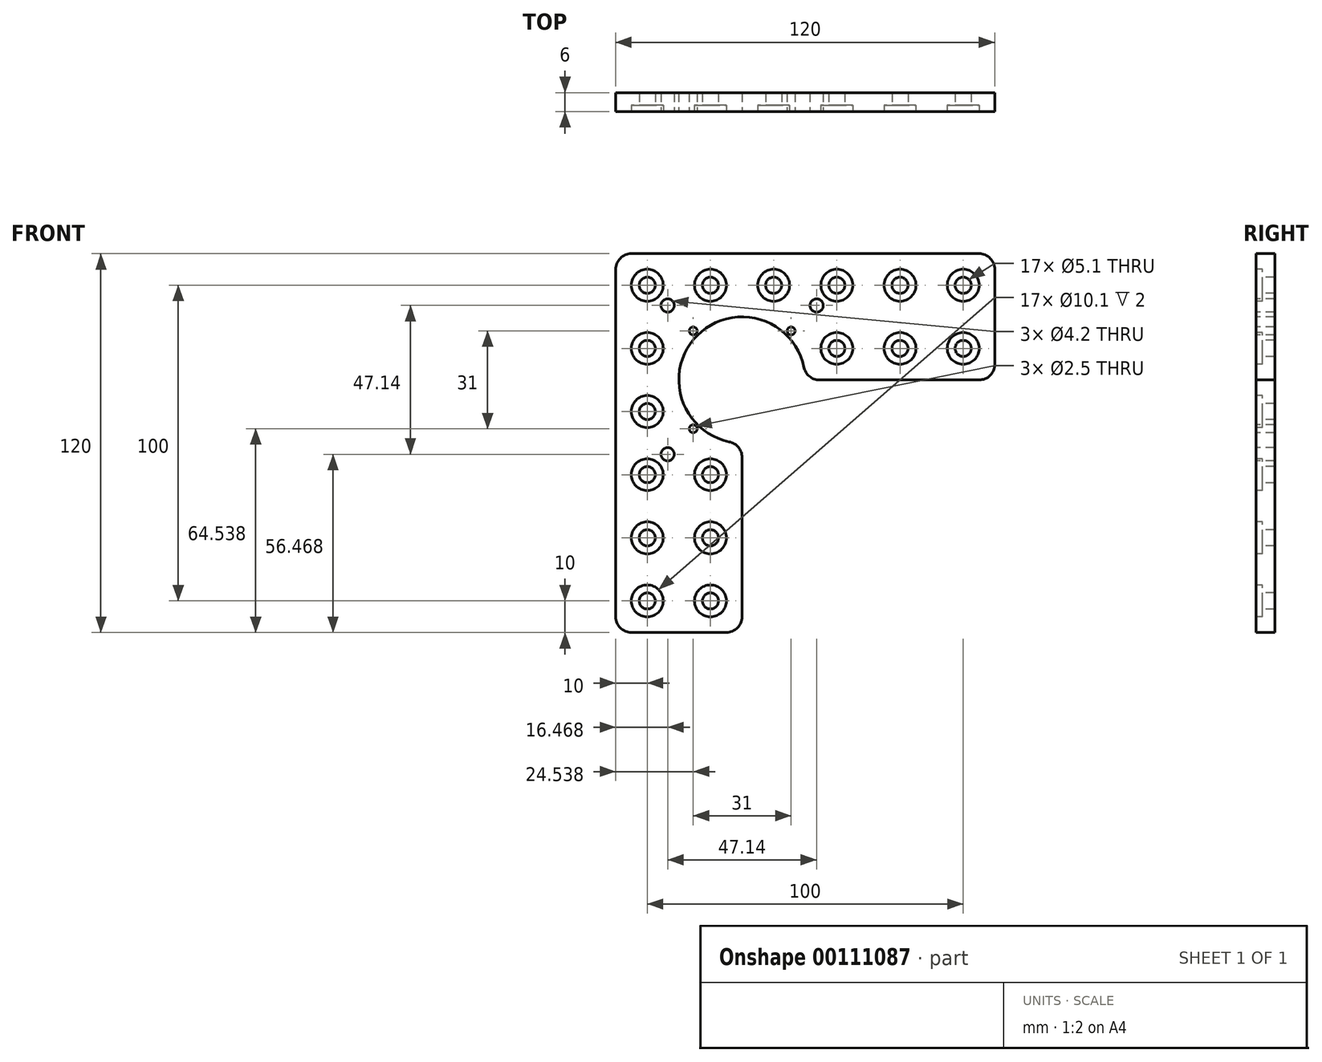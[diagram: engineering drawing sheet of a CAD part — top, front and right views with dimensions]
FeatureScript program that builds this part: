
annotation { "Feature Type Name" : "Feature", "Feature Type Description" : "" }
export const myFeature = defineFeature(function(context is Context, id is Id, definition is map)
    precondition{}
    {
        {
            var Q0;
            Q0=qCreatedBy(makeId("Front.planeOp"),FACE);
            var sketch = newSketch(context, id + "F0", { "sketchPlane" : qUnion([Q0])});
            skLineSegment(sketch, "E0.bottom", {"start": v(5, 0) * mm, "end": v(115, 0) * mm});
            skLineSegment(sketch, "E0.top", {"start": v(5, -120) * mm, "end": v(35, -120) * mm});
            skLineSegment(sketch, "E0.left", {"start": v(0, -5) * mm, "end": v(0, -115) * mm});
            skLineSegment(sketch, "E0.right", {"start": v(120, -5) * mm, "end": v(120, -35) * mm});
            skPoint(sketch, "E1", {"position": v(10, -10) * mm});
            skPoint(sketch, "E2", {"position": v(16.47, -16.4) * mm});
            skPoint(sketch, "E3", {"position": v(24.54, -24.46) * mm});
            skPoint(sketch, "E4.0.1.0", {"position": v(24.54, -55.46) * mm});
            skPoint(sketch, "E4.1.0.0", {"position": v(55.54, -24.46) * mm});
            skLineSegment(sketch, "E4.direction1", {"start": v(24.54, -24.46) * mm, "end": v(55.54, -24.46) * mm, "construction": true});
            skLineSegment(sketch, "E4.direction2", {"start": v(24.54, -24.46) * mm, "end": v(24.54, -55.46) * mm, "construction": true});
            skPoint(sketch, "E5.0.1.0", {"position": v(16.47, -63.53) * mm});
            skPoint(sketch, "E5.1.0.0", {"position": v(63.6, -16.4) * mm});
            skLineSegment(sketch, "E5.direction1", {"start": v(16.47, -16.4) * mm, "end": v(63.6, -16.4) * mm, "construction": true});
            skLineSegment(sketch, "E5.direction2", {"start": v(16.47, -16.4) * mm, "end": v(16.47, -63.53) * mm, "construction": true});
            skArc(sketch, "E6", {"start": v(59.6, -36) * mm, "mid": v(25.86, -25.86) * mm, "end": v(36, -59.6) * mm});
            skPoint(sketch, "E7.0.1.0", {"position": v(10, -30) * mm});
            skPoint(sketch, "E7.0.2.0", {"position": v(10, -50) * mm});
            skPoint(sketch, "E7.0.3.0", {"position": v(10, -70) * mm});
            skPoint(sketch, "E7.0.4.0", {"position": v(10, -90) * mm});
            skPoint(sketch, "E7.0.5.0", {"position": v(10, -110) * mm});
            skPoint(sketch, "E7.1.0.0", {"position": v(30, -10) * mm});
            skPoint(sketch, "E7.1.3.0", {"position": v(30, -70) * mm});
            skPoint(sketch, "E7.1.4.0", {"position": v(30, -90) * mm});
            skPoint(sketch, "E7.1.5.0", {"position": v(30, -110) * mm});
            skPoint(sketch, "E7.2.0.0", {"position": v(50, -10) * mm});
            skPoint(sketch, "E7.3.0.0", {"position": v(70, -10) * mm});
            skPoint(sketch, "E7.3.1.0", {"position": v(70, -30) * mm});
            skPoint(sketch, "E7.4.0.0", {"position": v(90, -10) * mm});
            skPoint(sketch, "E7.4.1.0", {"position": v(90, -30) * mm});
            skPoint(sketch, "E7.5.0.0", {"position": v(110, -10) * mm});
            skPoint(sketch, "E7.5.1.0", {"position": v(110, -30) * mm});
            skLineSegment(sketch, "E7.direction1", {"start": v(10, -10) * mm, "end": v(30, -10) * mm, "construction": true});
            skLineSegment(sketch, "E7.direction2", {"start": v(10, -10) * mm, "end": v(10, -30) * mm, "construction": true});
            skLineSegment(sketch, "E8.top", {"start": v(115, -40) * mm, "end": v(64.5, -40) * mm});
            skLineSegment(sketch, "E8.right", {"start": v(40, -115) * mm, "end": v(40, -64.5) * mm});
            skPoint(sketch, "E9.visualSharp", {"position": v(40, -120) * mm});
            skArc(sketch, "E9.filletArc", {"start": v(35, -120) * mm, "mid": v(38.54, -118.54) * mm, "end": v(40, -115) * mm});
            skPoint(sketch, "E10.visualSharp", {"position": v(120, -40) * mm});
            skArc(sketch, "E10.filletArc", {"start": v(115, -40) * mm, "mid": v(118.54, -38.54) * mm, "end": v(120, -35) * mm});
            skPoint(sketch, "E11.visualSharp", {"position": v(120, 0) * mm});
            skArc(sketch, "E11.filletArc", {"start": v(120, -5) * mm, "mid": v(118.54, -1.46) * mm, "end": v(115, 0) * mm});
            skPoint(sketch, "E12.visualSharp", {"position": v(0, -120) * mm});
            skArc(sketch, "E12.filletArc", {"start": v(0, -115) * mm, "mid": v(1.46, -118.54) * mm, "end": v(5, -120) * mm});
            skPoint(sketch, "E13.visualSharp", {"position": v(60, -40) * mm});
            skArc(sketch, "E13.filletArc", {"start": v(59.6, -36) * mm, "mid": v(61.33, -38.87) * mm, "end": v(64.5, -40) * mm});
            skPoint(sketch, "E14.visualSharp", {"position": v(40, -60) * mm});
            skArc(sketch, "E14.filletArc", {"start": v(40, -64.5) * mm, "mid": v(38.87, -61.33) * mm, "end": v(36, -59.6) * mm});
            skPoint(sketch, "E15.visualSharp", {"position": v(0, 0) * mm});
            skArc(sketch, "E15.filletArc", {"start": v(5, 0) * mm, "mid": v(1.46, -1.46) * mm, "end": v(0, -5) * mm});
            skSolve(sketch);
        }
        {
            var Q0;
            Q0=makeQuery(id+"F0.imprint","IMPRINT",FACE,{"disambiguationData":[TD([[makeQuery(id+"F0.imprint","IMPRINT",EDGE,{"derivedFrom":sQuery(id+"F0.wireOp",EDGE,"E0.bottom")}),-1.0]])]});
            extrude(context, id + "F1", {"entities" : qUnion([Q0]), "oppositeDirection" : true, "depth" : 6 * mm});
        }
        {
            var Q0;
            Q0=sQuery(id+"F0.wireOp",VERTEX,"E7.0.5.0");
            var Q1;
            Q1=sQuery(id+"F0.wireOp",VERTEX,"E7.1.5.0");
            var Q2;
            Q2=sQuery(id+"F0.wireOp",VERTEX,"E7.1.4.0");
            var Q3;
            Q3=sQuery(id+"F0.wireOp",VERTEX,"E7.0.4.0");
            var Q4;
            Q4=sQuery(id+"F0.wireOp",VERTEX,"E7.0.3.0");
            var Q5;
            Q5=sQuery(id+"F0.wireOp",VERTEX,"E7.1.3.0");
            var Q6;
            Q6=sQuery(id+"F0.wireOp",VERTEX,"E7.0.2.0");
            var Q7;
            Q7=sQuery(id+"F0.wireOp",VERTEX,"E7.0.1.0");
            var Q8;
            Q8=sQuery(id+"F0.wireOp",VERTEX,"E1");
            var Q9;
            Q9=sQuery(id+"F0.wireOp",VERTEX,"E7.1.0.0");
            var Q10;
            Q10=sQuery(id+"F0.wireOp",VERTEX,"E7.2.0.0");
            var Q11;
            Q11=sQuery(id+"F0.wireOp",VERTEX,"E7.3.0.0");
            var Q12;
            Q12=sQuery(id+"F0.wireOp",VERTEX,"E7.3.1.0");
            var Q13;
            Q13=sQuery(id+"F0.wireOp",VERTEX,"E7.4.1.0");
            var Q14;
            Q14=sQuery(id+"F0.wireOp",VERTEX,"E7.4.0.0");
            var Q15;
            Q15=sQuery(id+"F0.wireOp",VERTEX,"E7.5.0.0");
            var Q16;
            Q16=sQuery(id+"F0.wireOp",VERTEX,"E7.5.1.0");
            var Q17;
            Q17=makeQuery(id+"F1.opExtrude","SWEPT_BODY",BODY,{"disambiguationData":[OSD([sQuery(id+"F0.wireOp",EDGE,"E0.bottom"),sQuery(id+"F0.wireOp",EDGE,"E0.top"),sQuery(id+"F0.wireOp",EDGE,"E0.left"),sQuery(id+"F0.wireOp",EDGE,"E0.right"),sQuery(id+"F0.wireOp",EDGE,"E6"),sQuery(id+"F0.wireOp",EDGE,"E8.top"),sQuery(id+"F0.wireOp",EDGE,"E8.right"),sQuery(id+"F0.wireOp",EDGE,"E9.filletArc"),sQuery(id+"F0.wireOp",EDGE,"E10.filletArc"),sQuery(id+"F0.wireOp",EDGE,"E11.filletArc"),sQuery(id+"F0.wireOp",EDGE,"E12.filletArc"),sQuery(id+"F0.wireOp",EDGE,"E13.filletArc"),sQuery(id+"F0.wireOp",EDGE,"E14.filletArc"),sQuery(id+"F0.wireOp",EDGE,"E15.filletArc")])]});
            hole(context, id + "F2", {"style" : HoleStyle.C_BORE, "endStyle" : HoleEndStyle.THROUGH, "standardTappedOrClearance" : lookupTablePath({ "standard" : "ISO", "fit" : "Normal", "size" : "5.1", "type" : "Drilled" }), "standardBlindInLast" : lookupTablePath({ "fit" : "Standard", "standard" : "ISO", "size" : "5.1", "type" : "Drilled" }), "holeDiameter" : 5.1 * mm, "cBoreDiameter" : 10.1 * mm, "cBoreDepth" : 2 * mm, "locations" : qUnion([Q0, Q1, Q2, Q3, Q4, Q5, Q6, Q7, Q8, Q9, Q10, Q11, Q12, Q13, Q14, Q15, Q16]), "scope" : qUnion([Q17]), "isTappedThrough" : true});
        }
        {
            var Q0;
            Q0=sQuery(id+"F0.wireOp",VERTEX,"E5.direction1.start");
            var Q1;
            Q1=sQuery(id+"F0.wireOp",VERTEX,"E5.direction1.end");
            var Q2;
            Q2=sQuery(id+"F0.wireOp",VERTEX,"E5.0.1.0");
            var Q3;
            Q3=makeQuery(id+"F1.opExtrude","SWEPT_BODY",BODY,{"disambiguationData":[OSD([sQuery(id+"F0.wireOp",EDGE,"E0.bottom"),sQuery(id+"F0.wireOp",EDGE,"E0.top"),sQuery(id+"F0.wireOp",EDGE,"E0.left"),sQuery(id+"F0.wireOp",EDGE,"E0.right"),sQuery(id+"F0.wireOp",EDGE,"E6"),sQuery(id+"F0.wireOp",EDGE,"E8.top"),sQuery(id+"F0.wireOp",EDGE,"E8.right"),sQuery(id+"F0.wireOp",EDGE,"E9.filletArc"),sQuery(id+"F0.wireOp",EDGE,"E10.filletArc"),sQuery(id+"F0.wireOp",EDGE,"E11.filletArc"),sQuery(id+"F0.wireOp",EDGE,"E12.filletArc"),sQuery(id+"F0.wireOp",EDGE,"E13.filletArc"),sQuery(id+"F0.wireOp",EDGE,"E14.filletArc"),sQuery(id+"F0.wireOp",EDGE,"E15.filletArc")])]});
            hole(context, id + "F3", {"style" : HoleStyle.SIMPLE, "endStyle" : HoleEndStyle.THROUGH, "standardTappedOrClearance" : lookupTablePath({ "standard" : "ISO", "fit" : "Normal", "engagement" : "75%", "pitch" : "0.8 mm", "size" : "M5", "type" : "Tapped" }), "standardBlindInLast" : lookupTablePath({ "fit" : "Standard", "standard" : "ISO", "engagement" : "75%", "pitch" : "0.8 mm", "size" : "M5", "type" : "Tapped" }), "holeDiameter" : 4.2 * mm, "locations" : qUnion([Q0, Q1, Q2]), "scope" : qUnion([Q3]), "isTappedThrough" : true, "majorDiameter" : 5 * mm, "showTappedDepth" : true});
        }
        {
            var Q0;
            Q0=sQuery(id+"F0.wireOp",VERTEX,"E3");
            var Q1;
            Q1=sQuery(id+"F0.wireOp",VERTEX,"E4.direction1.end");
            var Q2;
            Q2=sQuery(id+"F0.wireOp",VERTEX,"E4.direction2.end");
            var Q3;
            Q3=makeQuery(id+"F1.opExtrude","SWEPT_BODY",BODY,{"disambiguationData":[OSD([sQuery(id+"F0.wireOp",EDGE,"E0.bottom"),sQuery(id+"F0.wireOp",EDGE,"E0.top"),sQuery(id+"F0.wireOp",EDGE,"E0.left"),sQuery(id+"F0.wireOp",EDGE,"E0.right"),sQuery(id+"F0.wireOp",EDGE,"E6"),sQuery(id+"F0.wireOp",EDGE,"E8.top"),sQuery(id+"F0.wireOp",EDGE,"E8.right"),sQuery(id+"F0.wireOp",EDGE,"E9.filletArc"),sQuery(id+"F0.wireOp",EDGE,"E10.filletArc"),sQuery(id+"F0.wireOp",EDGE,"E11.filletArc"),sQuery(id+"F0.wireOp",EDGE,"E12.filletArc"),sQuery(id+"F0.wireOp",EDGE,"E13.filletArc"),sQuery(id+"F0.wireOp",EDGE,"E14.filletArc"),sQuery(id+"F0.wireOp",EDGE,"E15.filletArc")])]});
            hole(context, id + "F4", {"style" : HoleStyle.SIMPLE, "endStyle" : HoleEndStyle.THROUGH, "standardTappedOrClearance" : lookupTablePath({ "standard" : "ISO", "fit" : "Normal", "engagement" : "75%", "pitch" : "0.5 mm", "size" : "M3", "type" : "Tapped" }), "standardBlindInLast" : lookupTablePath({ "fit" : "Standard", "standard" : "ISO", "engagement" : "75%", "pitch" : "0.5 mm", "size" : "M3", "type" : "Tapped" }), "holeDiameter" : 2.5 * mm, "locations" : qUnion([Q0, Q1, Q2]), "scope" : qUnion([Q3]), "isTappedThrough" : true, "majorDiameter" : 3 * mm, "showTappedDepth" : true});
        }
    });
